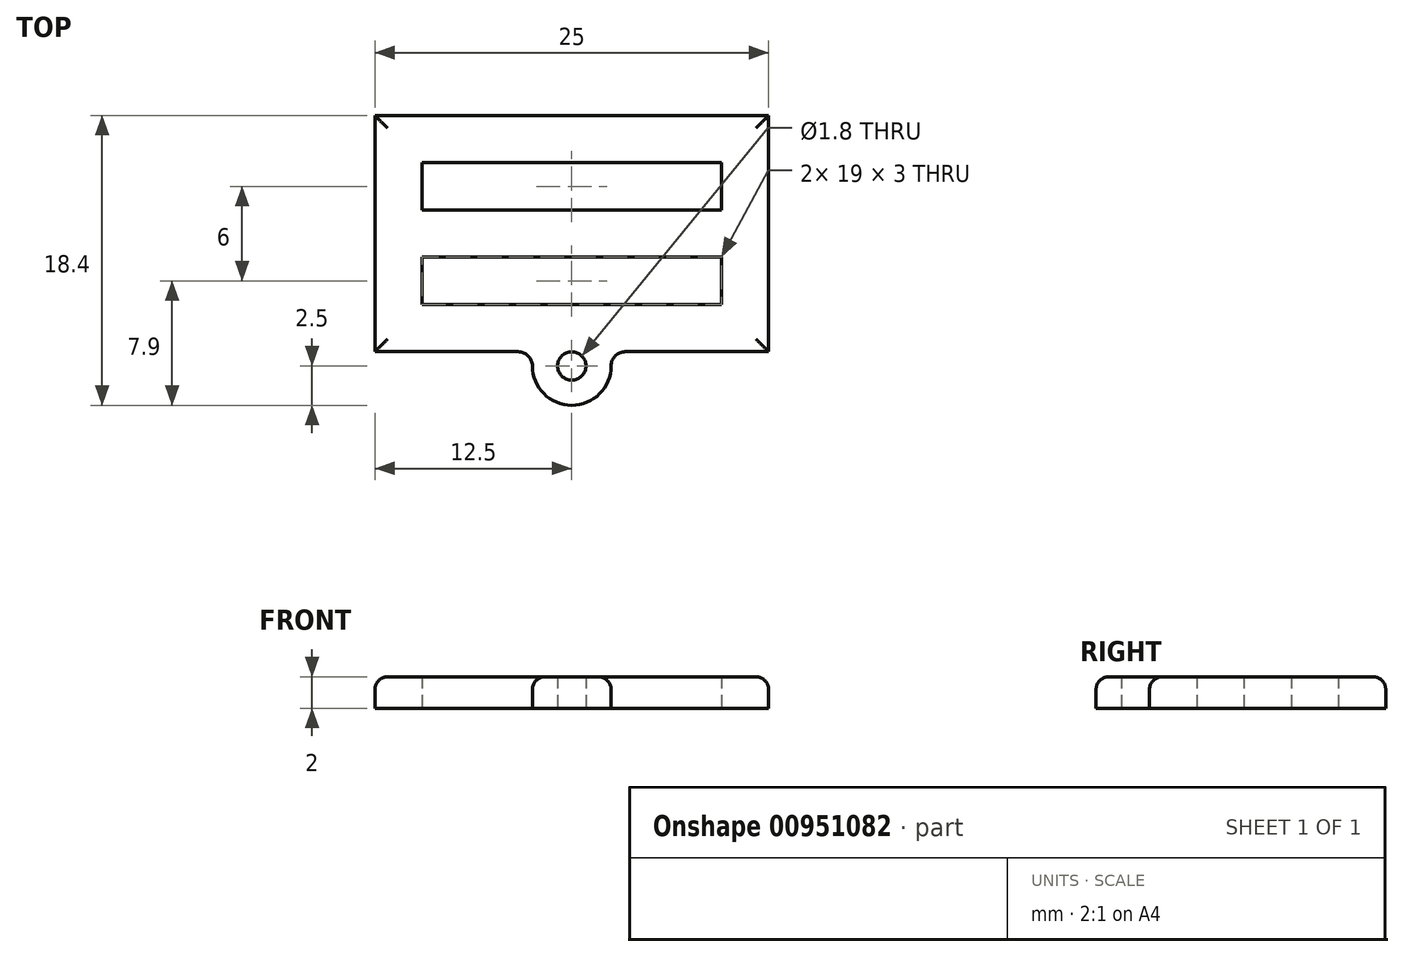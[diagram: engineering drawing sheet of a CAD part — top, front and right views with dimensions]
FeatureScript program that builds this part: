
annotation { "Feature Type Name" : "Feature", "Feature Type Description" : "" }
export const myFeature = defineFeature(function(context is Context, id is Id, definition is map)
    precondition{}
    {
        {
            var Q0;
            Q0=qCreatedBy(makeId("Top.planeOp"),FACE);
            var sketch = newSketch(context, id + "F0", { "sketchPlane" : qUnion([Q0])});
            skLineSegment(sketch, "E0.bottom", {"start": v(-12.5, 7.5) * mm, "end": v(12.5, 7.5) * mm});
            skLineSegment(sketch, "E0.top", {"start": v(-12.5, -7.5) * mm, "end": v(-2.5, -7.5) * mm});
            skLineSegment(sketch, "E0.left", {"start": v(-12.5, 7.5) * mm, "end": v(-12.5, -7.5) * mm});
            skLineSegment(sketch, "E0.right", {"start": v(12.5, 7.5) * mm, "end": v(12.5, -7.5) * mm});
            skLineSegment(sketch, "E1.bottom", {"start": v(-9.5, 4.5) * mm, "end": v(9.5, 4.5) * mm});
            skLineSegment(sketch, "E1.top", {"start": v(-9.5, 1.5) * mm, "end": v(9.5, 1.5) * mm});
            skLineSegment(sketch, "E1.left", {"start": v(-9.5, 4.5) * mm, "end": v(-9.5, 1.5) * mm});
            skLineSegment(sketch, "E1.right", {"start": v(9.5, 4.5) * mm, "end": v(9.5, 1.5) * mm});
            skLineSegment(sketch, "E2.0.1.0", {"start": v(-9.5, -1.5) * mm, "end": v(9.5, -1.5) * mm});
            skLineSegment(sketch, "E2.0.1.1", {"start": v(9.5, -1.5) * mm, "end": v(9.5, -4.5) * mm});
            skLineSegment(sketch, "E2.0.1.2", {"start": v(-9.5, -4.5) * mm, "end": v(9.5, -4.5) * mm});
            skLineSegment(sketch, "E2.0.1.3", {"start": v(-9.5, -1.5) * mm, "end": v(-9.5, -4.5) * mm});
            skLineSegment(sketch, "E2.direction1", {"start": v(-9.5, 4.5) * mm, "end": v(15.5, 4.5) * mm, "construction": true});
            skLineSegment(sketch, "E2.direction2", {"start": v(-9.5, 4.5) * mm, "end": v(-9.5, -1.5) * mm, "construction": true});
            skCircle(sketch, "E3", {"center": v(0, -8.4) * mm, "radius": 0.9 * mm});
            skArc(sketch, "E4", {"start": v(-2.5, -8.4) * mm, "mid": v(0, -10.9) * mm, "end": v(2.5, -8.4) * mm});
            skLineSegment(sketch, "E5", {"start": v(-5.4, -8.4) * mm, "end": v(5.7, -8.4) * mm, "construction": true});
            skLineSegment(sketch, "E6", {"start": v(-2.5, -8.4) * mm, "end": v(-2.5, -7.5) * mm});
            skLineSegment(sketch, "E7", {"start": v(2.5, -8.4) * mm, "end": v(2.5, -7.5) * mm});
            skLineSegment(sketch, "E8.trimOffspring", {"start": v(2.5, -7.5) * mm, "end": v(12.5, -7.5) * mm});
            skSolve(sketch);
        }
        {
            var Q0;
            Q0=makeQuery(id+"F0.imprint","IMPRINT",FACE,{"disambiguationData":[TD([[makeQuery(id+"F0.imprint","IMPRINT",EDGE,{"derivedFrom":sQuery(id+"F0.wireOp",EDGE,"E0.bottom")}),-1.0]])]});
            extrude(context, id + "F1", {"entities" : qUnion([Q0]), "depth" : 2 * mm, "offsetDistance" : 25 * mm});
        }
        {
            var Q0;
            Q0=makeQuery(id+"F1.opExtrude","SWEPT_EDGE",EDGE,{"disambiguationData":[OSD([sQuery(id+"F0.wireOp",EDGE,"E7"),sQuery(id+"F0.wireOp",EDGE,"E8.trimOffspring")])]});
            var Q1;
            Q1=makeQuery(id+"F1.opExtrude","SWEPT_EDGE",EDGE,{"disambiguationData":[OSD([sQuery(id+"F0.wireOp",EDGE,"E0.top"),sQuery(id+"F0.wireOp",EDGE,"E6")])]});
            fillet(context, id + "F2", {"entities" : qUnion([Q0, Q1]), "radius" : 0.9 * mm, "tangentPropagation" : true, "allowEdgeOverflow" : false});
        }
        {
            var Q0;
            Q0=makeQuery(id+"F1.opExtrude","CAP_EDGE",EDGE,{"disambiguationData":[OSD([sQuery(id+"F0.wireOp",EDGE,"E0.right")])],"isStart":false});
            var Q1;
            Q1=makeQuery(id+"F1.opExtrude","CAP_EDGE",EDGE,{"disambiguationData":[OSD([sQuery(id+"F0.wireOp",EDGE,"E8.trimOffspring")])],"isStart":false});
            var Q2;
            Q2=makeQuery(id+"F1.opExtrude","CAP_EDGE",EDGE,{"disambiguationData":[OSD([sQuery(id+"F0.wireOp",EDGE,"E0.left")])],"isStart":false});
            var Q3;
            Q3=makeQuery(id+"F1.opExtrude","CAP_EDGE",EDGE,{"disambiguationData":[OSD([sQuery(id+"F0.wireOp",EDGE,"E0.bottom")])],"isStart":false});
            fillet(context, id + "F3", {"entities" : qUnion([Q0, Q1, Q2, Q3]), "radius" : 0.8 * mm, "tangentPropagation" : true, "allowEdgeOverflow" : false});
        }
    });
